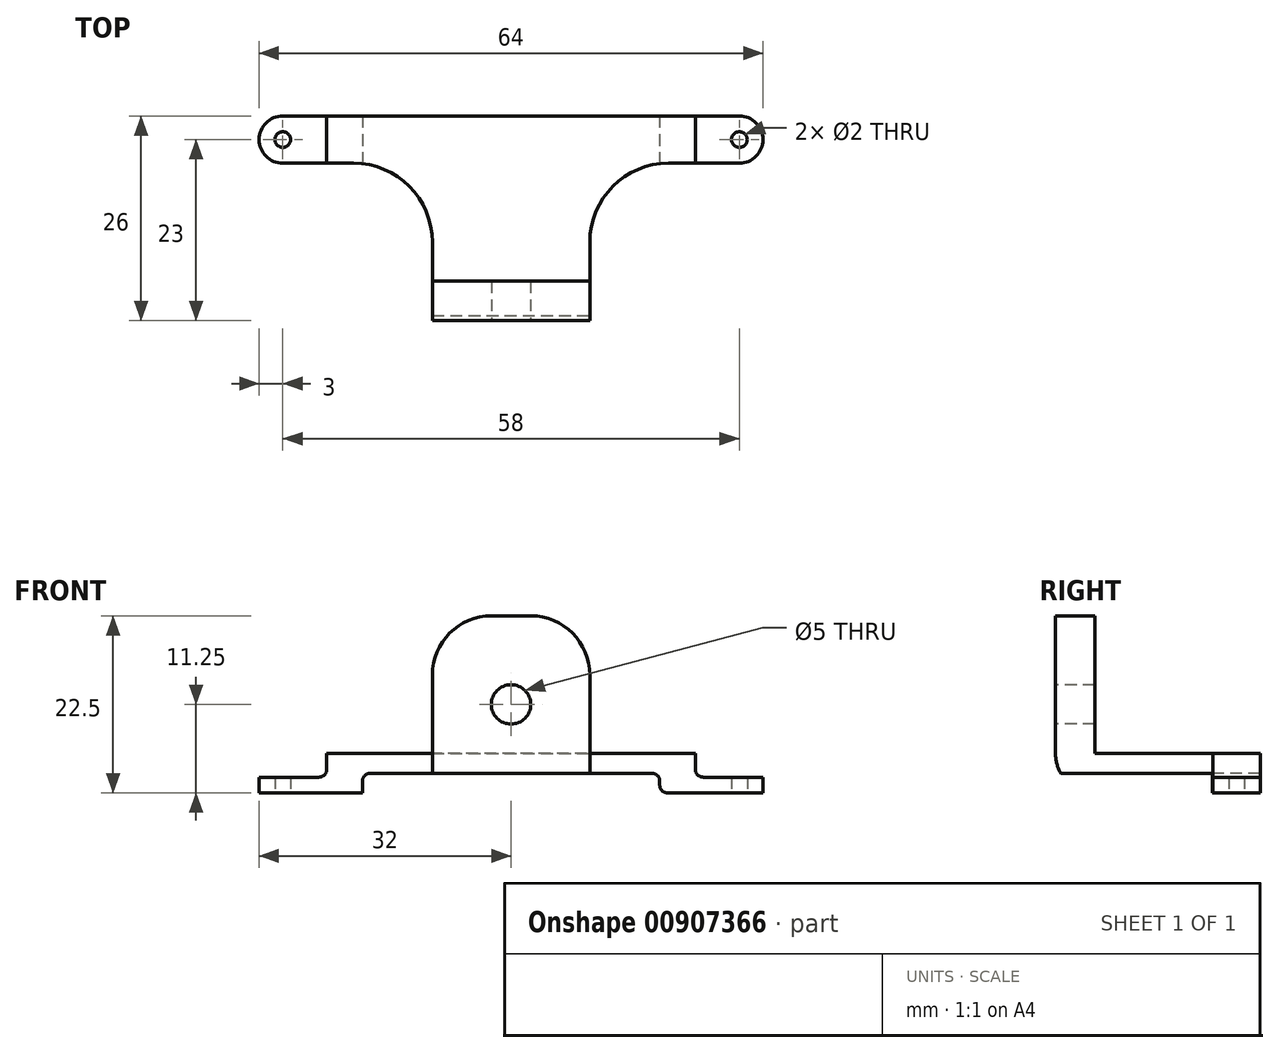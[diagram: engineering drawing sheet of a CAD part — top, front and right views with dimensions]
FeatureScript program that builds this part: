
annotation { "Feature Type Name" : "Feature", "Feature Type Description" : "" }
export const myFeature = defineFeature(function(context is Context, id is Id, definition is map)
    precondition{}
    {
        {
            var Q0;
            Q0=qCreatedBy(makeId("Top.planeOp"),FACE);
            var sketch = newSketch(context, id + "F0", { "sketchPlane" : qUnion([Q0])});
            skLineSegment(sketch, "E0.bottom", {"start": v(29, -3) * mm, "end": v(-29, -3) * mm});
            skLineSegment(sketch, "E0.top", {"start": v(29, 3) * mm, "end": v(-29, 3) * mm});
            skLineSegment(sketch, "E0.left", {"start": v(29, -3) * mm, "end": v(29, 3) * mm});
            skLineSegment(sketch, "E0.right", {"start": v(-29, -3) * mm, "end": v(-29, 3) * mm});
            skPoint(sketch, "E0.middle", {"position": v(0, 0) * mm});
            skLineSegment(sketch, "E1", {"start": v(-29, 0) * mm, "end": v(29, 0) * mm, "construction": true});
            skCircle(sketch, "E2", {"center": v(-29, 0) * mm, "radius": 3 * mm});
            skCircle(sketch, "E3", {"center": v(29, 0) * mm, "radius": 3 * mm});
            skCircle(sketch, "E4", {"center": v(-29, 0) * mm, "radius": 1 * mm});
            skCircle(sketch, "E5", {"center": v(29, 0) * mm, "radius": 1 * mm});
            skLineSegment(sketch, "E6", {"start": v(0, 0) * mm, "end": v(0, -13) * mm, "construction": true});
            skLineSegment(sketch, "E7.bottom", {"start": v(10, -3) * mm, "end": v(-10, -3) * mm});
            skLineSegment(sketch, "E7.top", {"start": v(10, -23) * mm, "end": v(-10, -23) * mm});
            skLineSegment(sketch, "E7.left", {"start": v(10, -3) * mm, "end": v(10, -23) * mm});
            skLineSegment(sketch, "E7.right", {"start": v(-10, -3) * mm, "end": v(-10, -23) * mm});
            skPoint(sketch, "E7.middle", {"position": v(0, -13) * mm});
            skSolve(sketch);
        }
        {
            var Q0;
            Q0=makeQuery(id+"F0.imprint","IMPRINT",FACE,{"disambiguationData":[TD([[makeQuery(id+"F0.imprint","IMPRINT",EDGE,{"derivedFrom":sQuery(id+"F0.wireOp",EDGE,"E7.top")}),-1.0]])]});
            var Q1;
            {var subQ0=sQuery(id+"F0.wireOp",EDGE,"E0.top");Q1=makeQuery(id+"F0.imprint","IMPRINT",FACE,{"disambiguationData":[TD([[makeQuery(id+"F0.imprint","IMPRINT",EDGE,{"derivedFrom":subQ0}),1.0]])]});}
            var Q2;
            {var subQ1=sQuery(id+"F0.wireOp",EDGE,"E0.right");var subQ3=sQuery(id+"F0.wireOp",EDGE,"E4");var subQ6=makeQuery(id+"F0.imprint","INTERSECT",VERTEX,{"disambiguationData":[OD(0.0)],"derivedFrom":[subQ1,subQ3]});Q2=makeQuery(id+"F0.imprint","IMPRINT",FACE,{"disambiguationData":[TD([[makeQuery(id+"F0.imprint","IMPRINT",EDGE,{"disambiguationData":[TD([[subQ6,-1.0]])],"derivedFrom":subQ3}),-1.0]])]});}
            var Q3;
            {var subQ1=sQuery(id+"F0.wireOp",EDGE,"E0.right");var subQ3=sQuery(id+"F0.wireOp",EDGE,"E4");var subQ6=makeQuery(id+"F0.imprint","INTERSECT",VERTEX,{"disambiguationData":[OD(0.0)],"derivedFrom":[subQ1,subQ3]});Q3=makeQuery(id+"F0.imprint","IMPRINT",FACE,{"disambiguationData":[TD([[makeQuery(id+"F0.imprint","IMPRINT",EDGE,{"disambiguationData":[TD([[subQ6,1.0]])],"derivedFrom":subQ3}),-1.0]])]});}
            var Q4;
            {var subQ1=sQuery(id+"F0.wireOp",EDGE,"E0.left");var subQ3=sQuery(id+"F0.wireOp",EDGE,"E5");var subQ6=makeQuery(id+"F0.imprint","INTERSECT",VERTEX,{"disambiguationData":[OD(0.0)],"derivedFrom":[subQ1,subQ3]});Q4=makeQuery(id+"F0.imprint","IMPRINT",FACE,{"disambiguationData":[TD([[makeQuery(id+"F0.imprint","IMPRINT",EDGE,{"disambiguationData":[TD([[subQ6,-1.0]])],"derivedFrom":subQ3}),-1.0]])]});}
            var Q5;
            {var subQ1=sQuery(id+"F0.wireOp",EDGE,"E0.left");var subQ3=sQuery(id+"F0.wireOp",EDGE,"E5");var subQ6=makeQuery(id+"F0.imprint","INTERSECT",VERTEX,{"disambiguationData":[OD(0.0)],"derivedFrom":[subQ1,subQ3]});Q5=makeQuery(id+"F0.imprint","IMPRINT",FACE,{"disambiguationData":[TD([[makeQuery(id+"F0.imprint","IMPRINT",EDGE,{"disambiguationData":[TD([[subQ6,1.0]])],"derivedFrom":subQ3}),-1.0]])]});}
            extrude(context, id + "F1", {"entities" : qUnion([Q0, Q1, Q2, Q3, Q4, Q5]), "depth" : 5 * mm, "offsetDistance" : 25 * mm});
        }
        {
            var Q0;
            Q0=makeQuery(id+"F1.opExtrude","CAP_FACE",FACE,{"disambiguationData":[OSD([sQuery(id+"F0.wireOp",EDGE,"E0.bottom"),sQuery(id+"F0.wireOp",EDGE,"E0.top"),sQuery(id+"F0.wireOp",EDGE,"E2"),sQuery(id+"F0.wireOp",EDGE,"E3"),sQuery(id+"F0.wireOp",EDGE,"E4"),sQuery(id+"F0.wireOp",EDGE,"E5"),sQuery(id+"F0.wireOp",EDGE,"E7.top"),sQuery(id+"F0.wireOp",EDGE,"E7.left"),sQuery(id+"F0.wireOp",EDGE,"E7.right")])],"isStart":false});
            var sketch = newSketch(context, id + "F2", { "sketchPlane" : qUnion([Q0])});
            skLineSegment(sketch, "E8.bottom", {"start": v(-10, -23) * mm, "end": v(10, -23) * mm});
            skLineSegment(sketch, "E8.top", {"start": v(-10, -18) * mm, "end": v(10, -18) * mm});
            skLineSegment(sketch, "E8.left", {"start": v(-10, -23) * mm, "end": v(-10, -18) * mm});
            skLineSegment(sketch, "E8.right", {"start": v(10, -23) * mm, "end": v(10, -18) * mm});
            skSolve(sketch);
        }
        {
            var Q0;
            Q0=makeQuery(id+"F2.imprint","IMPRINT",FACE,{"disambiguationData":[TD([[makeQuery(id+"F2.imprint","IMPRINT",EDGE,{"derivedFrom":sQuery(id+"F2.wireOp",EDGE,"E8.bottom")}),-1.0]])]});
            extrude(context, id + "F3", {"entities" : qUnion([Q0]), "operationType" : NewBodyOperationType.ADD, "depth" : 17.5 * mm, "offsetDistance" : 25 * mm});
        }
        {
            var Q0;
            Q0=makeQuery(id+"F3.boolean.opBoolean","MERGE",FACE,{"derivedFrom":[makeQuery(id+"F1.opExtrude","SWEPT_FACE",FACE,{"disambiguationData":[OSD([sQuery(id+"F0.wireOp",EDGE,"E7.top")])]}),makeQuery(id+"F3.opExtrude","SWEPT_FACE",FACE,{"disambiguationData":[OSD([sQuery(id+"F2.wireOp",EDGE,"E8.bottom")])]})]});
            var sketch = newSketch(context, id + "F4", { "sketchPlane" : qUnion([Q0])});
            skLineSegment(sketch, "E9.bottom", {"start": v(-10, 22.5) * mm, "end": v(10, 22.5) * mm});
            skLineSegment(sketch, "E9.top", {"start": v(-10, 0) * mm, "end": v(10, 0) * mm});
            skLineSegment(sketch, "E9.left", {"start": v(-10, 22.5) * mm, "end": v(-10, 0) * mm});
            skLineSegment(sketch, "E9.right", {"start": v(10, 22.5) * mm, "end": v(10, 0) * mm});
            skLineSegment(sketch, "E10", {"start": v(0, 22.5) * mm, "end": v(0, 0) * mm, "construction": true});
            skCircle(sketch, "E11", {"center": v(0, 11.25) * mm, "radius": 2.5 * mm});
            skSolve(sketch);
        }
        {
            var Q0;
            Q0=makeQuery(id+"F4.imprint","IMPRINT",FACE,{"disambiguationData":[TD([[makeQuery(id+"F4.imprint","IMPRINT",EDGE,{"derivedFrom":sQuery(id+"F4.wireOp",EDGE,"E11")}),1.0]])]});
            var Q1;
            Q1=makeQuery(id+"F3.opExtrude","SWEPT_FACE",FACE,{"disambiguationData":[OSD([sQuery(id+"F2.wireOp",EDGE,"E8.top")])]});
            extrude(context, id + "F5", {"entities" : qUnion([Q0]), "operationType" : NewBodyOperationType.REMOVE, "endBound" : BoundingType.UP_TO_SURFACE, "oppositeDirection" : true, "depth" : 25 * mm, "endBoundEntityFace" : qUnion([Q1]), "offsetDistance" : 25 * mm});
        }
        {
            var Q0;
            Q0=makeQuery(id+"F3.opExtrude","CAP_EDGE",EDGE,{"disambiguationData":[OSD([sQuery(id+"F2.wireOp",EDGE,"E8.right")])],"isStart":false});
            var Q1;
            Q1=makeQuery(id+"F3.opExtrude","CAP_EDGE",EDGE,{"disambiguationData":[OSD([sQuery(id+"F2.wireOp",EDGE,"E8.left")])],"isStart":false});
            fillet(context, id + "F6", {"entities" : qUnion([Q0, Q1]), "tangentPropagation" : true, "radius" : 7.5 * mm, "defaultsChanged" : true, "vertexSettings" : [], "allowEdgeOverflow" : false});
        }
        {
            var Q0;
            Q0=makeQuery(id+"F3.opExtrude","CAP_EDGE",EDGE,{"disambiguationData":[OSD([sQuery(id+"F2.wireOp",EDGE,"E8.top")])],"isStart":true});
            var Q1;
            Q1=makeQuery(id+"F1.opExtrude","CAP_EDGE",EDGE,{"disambiguationData":[OSD([sQuery(id+"F0.wireOp",EDGE,"E7.top")])],"isStart":true});
            fillet(context, id + "F7", {"entities" : qUnion([Q0, Q1]), "tangentPropagation" : true, "radius" : 5 * mm, "defaultsChanged" : false, "vertexSettings" : [], "allowEdgeOverflow" : false});
        }
        {
            var Q0;
            Q0=makeQuery(id+"F1.opExtrude","SWEPT_EDGE",EDGE,{"disambiguationData":[OSD([sQuery(id+"F0.wireOp",EDGE,"E0.bottom"),sQuery(id+"F0.wireOp",EDGE,"E7.left")])]});
            var Q1;
            Q1=makeQuery(id+"F1.opExtrude","SWEPT_EDGE",EDGE,{"disambiguationData":[OSD([sQuery(id+"F0.wireOp",EDGE,"E0.bottom"),sQuery(id+"F0.wireOp",EDGE,"E7.right")])]});
            fillet(context, id + "F8", {"entities" : qUnion([Q0, Q1]), "tangentPropagation" : true, "radius" : 10 * mm, "defaultsChanged" : true, "vertexSettings" : [], "allowEdgeOverflow" : false});
        }
        {
            var Q0;
            Q0=makeQuery(id+"F1.opExtrude","CAP_FACE",FACE,{"disambiguationData":[OSD([sQuery(id+"F0.wireOp",EDGE,"E0.bottom"),sQuery(id+"F0.wireOp",EDGE,"E0.top"),sQuery(id+"F0.wireOp",EDGE,"E2"),sQuery(id+"F0.wireOp",EDGE,"E3"),sQuery(id+"F0.wireOp",EDGE,"E4"),sQuery(id+"F0.wireOp",EDGE,"E5"),sQuery(id+"F0.wireOp",EDGE,"E7.top"),sQuery(id+"F0.wireOp",EDGE,"E7.left"),sQuery(id+"F0.wireOp",EDGE,"E7.right")])],"isStart":true});
            var sketch = newSketch(context, id + "F9", { "sketchPlane" : qUnion([Q0])});
            skLineSegment(sketch, "E12.bottom", {"start": v(18.88, -26.94) * mm, "end": v(-18.88, -26.94) * mm});
            skLineSegment(sketch, "E12.top", {"start": v(18.88, 26.94) * mm, "end": v(-18.88, 26.94) * mm});
            skLineSegment(sketch, "E12.left", {"start": v(18.88, -26.94) * mm, "end": v(18.88, 26.94) * mm});
            skLineSegment(sketch, "E12.right", {"start": v(-18.88, -26.94) * mm, "end": v(-18.88, 26.94) * mm});
            skPoint(sketch, "E12.middle", {"position": v(0, 0) * mm});
            skSolve(sketch);
        }
        {
            var Q0;
            {var subQ0=sQuery(id+"F0.wireOp",EDGE,"E7.left");var subQ1=makeQuery(id+"F1.opExtrude","CAP_EDGE",EDGE,{"disambiguationData":[OSD([subQ0])],"isStart":true});Q0=makeQuery(id+"F9.imprint","IMPRINT",FACE,{"disambiguationData":[TD([[makeQuery(id+"F9.imprint","IMPRINT",EDGE,{"derivedFrom":subQ1}),1.0]])]});}
            var Q1;
            {var subQ5=sQuery(id+"F9.wireOp",EDGE,"E12.top");Q1=makeQuery(id+"F9.imprint","IMPRINT",FACE,{"disambiguationData":[TD([[makeQuery(id+"F9.imprint","IMPRINT",EDGE,{"derivedFrom":subQ5}),1.0]])]});}
            extrude(context, id + "F10", {"entities" : qUnion([Q0, Q1]), "operationType" : NewBodyOperationType.REMOVE, "oppositeDirection" : true, "depth" : 2.5 * mm, "offsetDistance" : 25 * mm});
        }
        {
            var Q0;
            Q0=makeQuery(id+"F1.opExtrude","CAP_FACE",FACE,{"disambiguationData":[OSD([sQuery(id+"F0.wireOp",EDGE,"E0.bottom"),sQuery(id+"F0.wireOp",EDGE,"E0.top"),sQuery(id+"F0.wireOp",EDGE,"E2"),sQuery(id+"F0.wireOp",EDGE,"E3"),sQuery(id+"F0.wireOp",EDGE,"E4"),sQuery(id+"F0.wireOp",EDGE,"E5"),sQuery(id+"F0.wireOp",EDGE,"E7.top"),sQuery(id+"F0.wireOp",EDGE,"E7.left"),sQuery(id+"F0.wireOp",EDGE,"E7.right")])],"isStart":false});
            var sketch = newSketch(context, id + "F11", { "sketchPlane" : qUnion([Q0])});
            skLineSegment(sketch, "E13.bottom", {"start": v(23.41, -9.57) * mm, "end": v(-23.41, -9.57) * mm});
            skLineSegment(sketch, "E13.top", {"start": v(23.41, 9.57) * mm, "end": v(-23.41, 9.57) * mm});
            skLineSegment(sketch, "E13.left", {"start": v(23.41, -9.57) * mm, "end": v(23.41, 9.57) * mm});
            skLineSegment(sketch, "E13.right", {"start": v(-23.41, -9.57) * mm, "end": v(-23.41, 9.57) * mm});
            skPoint(sketch, "E13.middle", {"position": v(0, 0) * mm});
            skLineSegment(sketch, "E14.bottom", {"start": v(23.41, 9.57) * mm, "end": v(36.42, 9.57) * mm});
            skLineSegment(sketch, "E14.top", {"start": v(23.41, -9.57) * mm, "end": v(36.42, -9.57) * mm});
            skLineSegment(sketch, "E14.left", {"start": v(23.41, 9.57) * mm, "end": v(23.41, -9.57) * mm});
            skLineSegment(sketch, "E14.right", {"start": v(36.42, 9.57) * mm, "end": v(36.42, -9.57) * mm});
            skLineSegment(sketch, "E15.bottom", {"start": v(-23.41, 9.57) * mm, "end": v(-36.01, 9.57) * mm});
            skLineSegment(sketch, "E15.top", {"start": v(-23.41, -9.57) * mm, "end": v(-36.01, -9.57) * mm});
            skLineSegment(sketch, "E15.left", {"start": v(-23.41, 9.57) * mm, "end": v(-23.41, -9.57) * mm});
            skLineSegment(sketch, "E15.right", {"start": v(-36.01, 9.57) * mm, "end": v(-36.01, -9.57) * mm});
            skSolve(sketch);
        }
        {
            var Q0;
            {var subQ0=sQuery(id+"F11.wireOp",EDGE,"E15.bottom");Q0=makeQuery(id+"F11.imprint","IMPRINT",FACE,{"disambiguationData":[TD([[makeQuery(id+"F11.imprint","IMPRINT",EDGE,{"derivedFrom":subQ0}),1.0]])]});}
            var Q1;
            {var subQ0=sQuery(id+"F0.wireOp",EDGE,"E2");var subQ1=makeQuery(id+"F1.opExtrude","CAP_EDGE",EDGE,{"disambiguationData":[OSD([subQ0])],"isStart":false});Q1=makeQuery(id+"F11.imprint","IMPRINT",FACE,{"disambiguationData":[TD([[makeQuery(id+"F11.imprint","IMPRINT",EDGE,{"derivedFrom":subQ1}),1.0]])]});}
            var Q2;
            {var subQ0=sQuery(id+"F0.wireOp",EDGE,"E3");var subQ1=makeQuery(id+"F1.opExtrude","CAP_EDGE",EDGE,{"disambiguationData":[OSD([subQ0])],"isStart":false});Q2=makeQuery(id+"F11.imprint","IMPRINT",FACE,{"disambiguationData":[TD([[makeQuery(id+"F11.imprint","IMPRINT",EDGE,{"derivedFrom":subQ1}),1.0]])]});}
            var Q3;
            {var subQ0=sQuery(id+"F11.wireOp",EDGE,"E14.bottom");Q3=makeQuery(id+"F11.imprint","IMPRINT",FACE,{"disambiguationData":[TD([[makeQuery(id+"F11.imprint","IMPRINT",EDGE,{"derivedFrom":subQ0}),-1.0]])]});}
            extrude(context, id + "F12", {"entities" : qUnion([Q0, Q1, Q2, Q3]), "operationType" : NewBodyOperationType.REMOVE, "oppositeDirection" : true, "depth" : 3 * mm, "offsetDistance" : 25 * mm});
        }
        {
            var Q0;
            Q0=makeQuery(id+"F12.boolean.opBoolean","COPY",EDGE,{"derivedFrom":makeQuery(id+"F12.opExtrude","CAP_EDGE",EDGE,{"disambiguationData":[OSD([sQuery(id+"F11.wireOp",EDGE,"E13.right")])],"isStart":true})});
            var Q1;
            Q1=makeQuery(id+"F12.boolean.opBoolean","COPY",EDGE,{"derivedFrom":makeQuery(id+"F12.opExtrude","CAP_EDGE",EDGE,{"disambiguationData":[OSD([sQuery(id+"F11.wireOp",EDGE,"E13.right")])],"isStart":false})});
            var Q2;
            Q2=makeQuery(id+"F10.boolean.opBoolean","COPY",EDGE,{"derivedFrom":makeQuery(id+"F10.opExtrude","CAP_EDGE",EDGE,{"disambiguationData":[OSD([sQuery(id+"F9.wireOp",EDGE,"E12.right")])],"isStart":true})});
            var Q3;
            Q3=makeQuery(id+"F10.boolean.opBoolean","COPY",EDGE,{"derivedFrom":makeQuery(id+"F10.opExtrude","CAP_EDGE",EDGE,{"disambiguationData":[OSD([sQuery(id+"F9.wireOp",EDGE,"E12.right")])],"isStart":false})});
            var Q4;
            Q4=makeQuery(id+"F10.boolean.opBoolean","COPY",EDGE,{"derivedFrom":makeQuery(id+"F10.opExtrude","CAP_EDGE",EDGE,{"disambiguationData":[OSD([sQuery(id+"F9.wireOp",EDGE,"E12.left")])],"isStart":false})});
            var Q5;
            Q5=makeQuery(id+"F10.boolean.opBoolean","COPY",EDGE,{"derivedFrom":makeQuery(id+"F10.opExtrude","CAP_EDGE",EDGE,{"disambiguationData":[OSD([sQuery(id+"F9.wireOp",EDGE,"E12.left")])],"isStart":true})});
            var Q6;
            Q6=makeQuery(id+"F12.boolean.opBoolean","COPY",EDGE,{"derivedFrom":makeQuery(id+"F12.opExtrude","CAP_EDGE",EDGE,{"disambiguationData":[OSD([sQuery(id+"F11.wireOp",EDGE,"E13.left")])],"isStart":true})});
            var Q7;
            Q7=makeQuery(id+"F12.boolean.opBoolean","COPY",EDGE,{"derivedFrom":makeQuery(id+"F12.opExtrude","CAP_EDGE",EDGE,{"disambiguationData":[OSD([sQuery(id+"F11.wireOp",EDGE,"E13.left")])],"isStart":false})});
            fillet(context, id + "F13", {"entities" : qUnion([Q0, Q1, Q2, Q3, Q4, Q5, Q6, Q7]), "tangentPropagation" : true, "radius" : 1 * mm, "defaultsChanged" : false, "vertexSettings" : [], "allowEdgeOverflow" : false});
        }
    });
